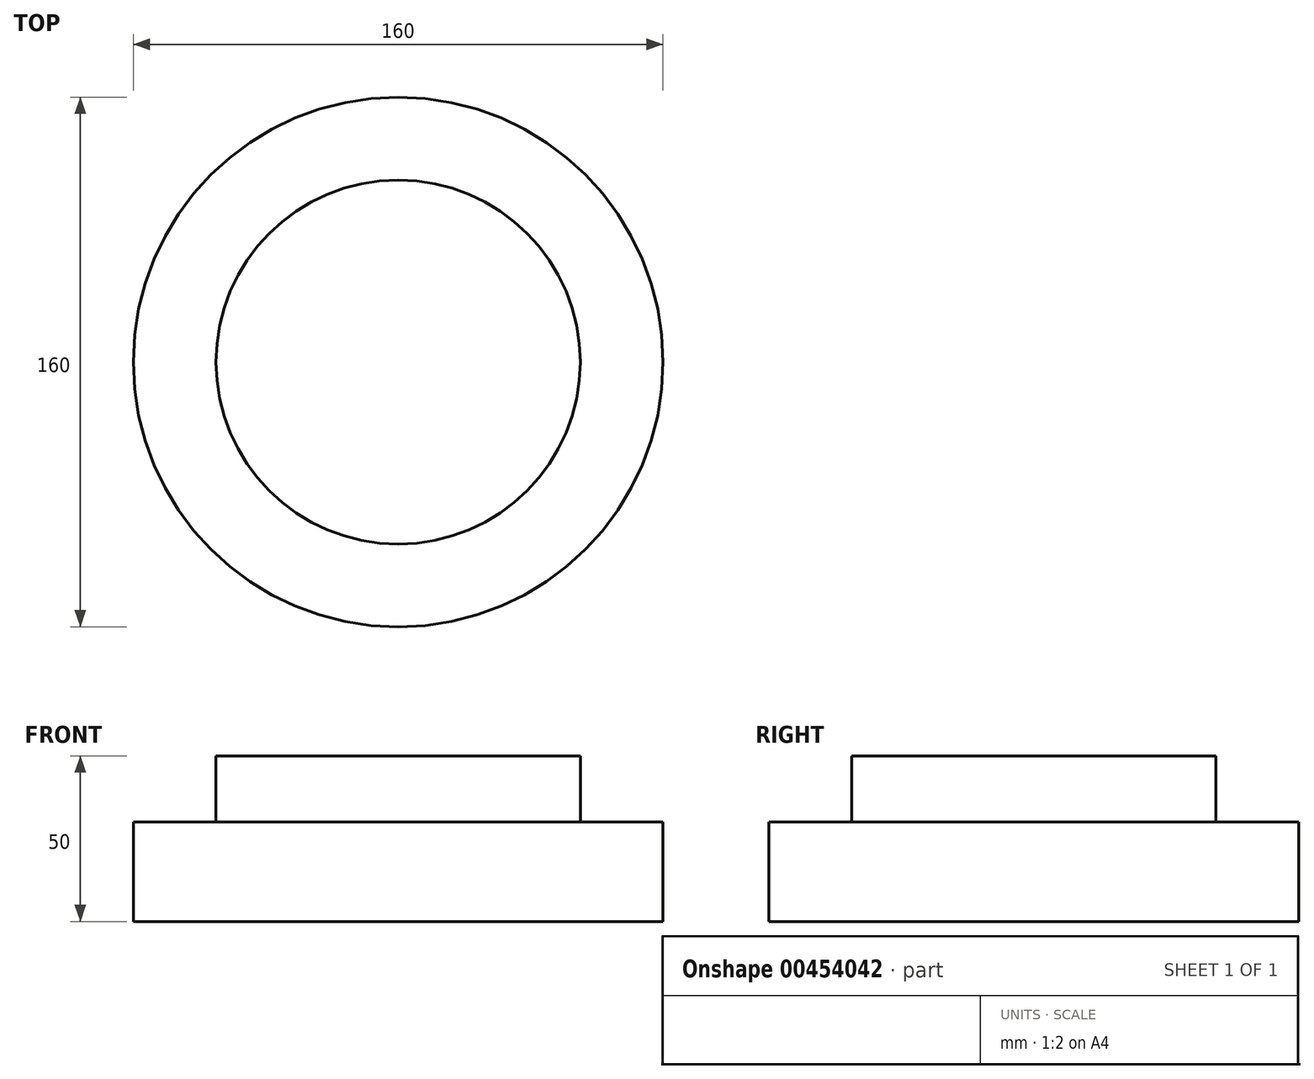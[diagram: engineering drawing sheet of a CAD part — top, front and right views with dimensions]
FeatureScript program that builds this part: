
annotation { "Feature Type Name" : "Feature", "Feature Type Description" : "" }
export const myFeature = defineFeature(function(context is Context, id is Id, definition is map)
    precondition{}
    {
        {
            var Q0;
            Q0=qCreatedBy(makeId("Front.planeOp"),FACE);
            var sketch = newSketch(context, id + "F0", { "sketchPlane" : qUnion([Q0])});
            skLineSegment(sketch, "E0.bottom", {"start": v(0, 0) * mm, "end": v(-80, 0) * mm});
            skLineSegment(sketch, "E0.top", {"start": v(0, 50) * mm, "end": v(-80, 50) * mm});
            skLineSegment(sketch, "E0.left", {"start": v(0, 0) * mm, "end": v(0, 50) * mm});
            skLineSegment(sketch, "E0.right", {"start": v(-80, 0) * mm, "end": v(-80, 50) * mm});
            skSolve(sketch);
        }
        {
            var Q0;
            Q0=makeQuery(id+"F0.imprint","IMPRINT",FACE,{"disambiguationData":[TD([[makeQuery(id+"F0.imprint","IMPRINT",EDGE,{"derivedFrom":sQuery(id+"F0.wireOp",EDGE,"E0.bottom")}),-1.0]])]});
            var Q1;
            Q1=sQuery(id+"F0.wireOp",EDGE,"E0.left");
            revolve(context, id + "F1", {"entities" : qUnion([Q0]), "axis" : qUnion([Q1]), "revolveType" : RevolveType.FULL});
        }
        {
            var Q0;
            Q0=qCreatedBy(makeId("Front.planeOp"),FACE);
            var sketch = newSketch(context, id + "F2", { "sketchPlane" : qUnion([Q0])});
            skLineSegment(sketch, "E1", {"start": v(0, 49.13) * mm, "end": v(0, 28.09) * mm});
            skSolve(sketch);
        }
        {
            var Q0;
            Q0=qCreatedBy(makeId("Front.planeOp"),FACE);
            var sketch = newSketch(context, id + "F3", { "sketchPlane" : qUnion([Q0])});
            skLineSegment(sketch, "E2.bottom", {"start": v(-86, 60) * mm, "end": v(-55, 60) * mm});
            skLineSegment(sketch, "E2.top", {"start": v(-86, 30) * mm, "end": v(-55, 30) * mm});
            skLineSegment(sketch, "E2.left", {"start": v(-86, 60) * mm, "end": v(-86, 30) * mm});
            skLineSegment(sketch, "E2.right", {"start": v(-55, 60) * mm, "end": v(-55, 30) * mm});
            skSolve(sketch);
        }
        {
            var Q0;
            Q0=makeQuery(id+"F3.imprint","IMPRINT",FACE,{"disambiguationData":[TD([[makeQuery(id+"F3.imprint","IMPRINT",EDGE,{"derivedFrom":sQuery(id+"F3.wireOp",EDGE,"E2.bottom")}),-1.0]])]});
            var Q1;
            Q1=sQuery(id+"F2.wireOp",EDGE,"E1");
            revolve(context, id + "F4", {"operationType" : NewBodyOperationType.REMOVE, "entities" : qUnion([Q0]), "axis" : qUnion([Q1]), "revolveType" : RevolveType.FULL, "oppositeDirection" : true});
        }
    });
